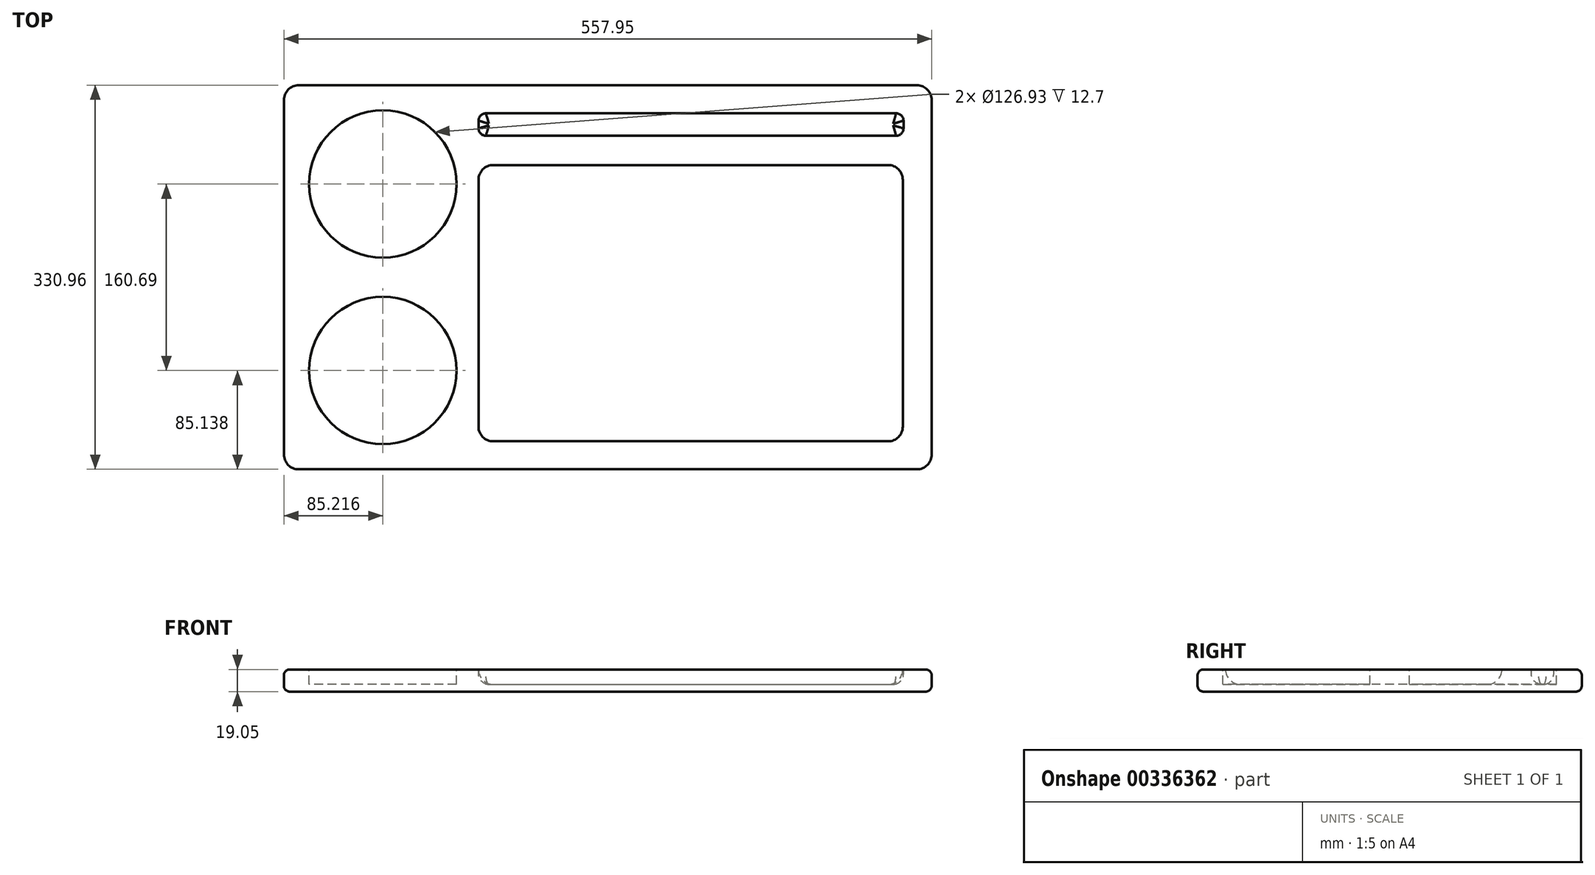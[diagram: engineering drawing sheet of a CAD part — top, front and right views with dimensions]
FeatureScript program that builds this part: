
annotation { "Feature Type Name" : "Feature", "Feature Type Description" : "" }
export const myFeature = defineFeature(function(context is Context, id is Id, definition is map)
    precondition{}
    {
        {
            var Q0;
            Q0=qCreatedBy(makeId("Top.planeOp"),FACE);
            var sketch = newSketch(context, id + "F0", { "sketchPlane" : qUnion([Q0])});
            skLineSegment(sketch, "E0.bottom", {"start": v(-154.97, 103.5) * mm, "end": v(402.98, 103.5) * mm});
            skLineSegment(sketch, "E0.top", {"start": v(-154.97, -227.46) * mm, "end": v(402.98, -227.46) * mm});
            skLineSegment(sketch, "E0.left", {"start": v(-154.97, 103.5) * mm, "end": v(-154.97, -227.46) * mm});
            skLineSegment(sketch, "E0.right", {"start": v(402.98, 103.5) * mm, "end": v(402.98, -227.46) * mm});
            skSolve(sketch);
        }
        {
            var Q0;
            Q0=makeQuery(id+"F0.imprint","IMPRINT",FACE,{"disambiguationData":[TD([[makeQuery(id+"F0.imprint","IMPRINT",EDGE,{"derivedFrom":sQuery(id+"F0.wireOp",EDGE,"E0.top")}),1.0]])]});
            extrude(context, id + "F1", {"entities" : qUnion([Q0]), "depth" : 19.05 * mm});
        }
        {
            var Q0;
            Q0=makeQuery(id+"F1.opExtrude","SWEPT_EDGE",EDGE,{"disambiguationData":[OSD([sQuery(id+"F0.wireOp",EDGE,"E0.top"),sQuery(id+"F0.wireOp",EDGE,"E0.left")])]});
            var Q1;
            Q1=makeQuery(id+"F1.opExtrude","SWEPT_EDGE",EDGE,{"disambiguationData":[OSD([sQuery(id+"F0.wireOp",EDGE,"E0.top"),sQuery(id+"F0.wireOp",EDGE,"E0.right")])]});
            var Q2;
            Q2=makeQuery(id+"F1.opExtrude","SWEPT_EDGE",EDGE,{"disambiguationData":[OSD([sQuery(id+"F0.wireOp",EDGE,"E0.bottom"),sQuery(id+"F0.wireOp",EDGE,"E0.right")])]});
            var Q3;
            Q3=makeQuery(id+"F1.opExtrude","SWEPT_EDGE",EDGE,{"disambiguationData":[OSD([sQuery(id+"F0.wireOp",EDGE,"E0.left"),sQuery(id+"F0.wireOp",EDGE,"E0.bottom")])]});
            fillet(context, id + "F2", {"entities" : qUnion([Q0, Q1, Q2, Q3]), "radius" : 12.7 * mm, "tangentPropagation" : true, "allowEdgeOverflow" : false});
        }
        {
            var Q0;
            Q0=makeQuery(id+"F1.opExtrude","CAP_EDGE",EDGE,{"disambiguationData":[OSD([sQuery(id+"F0.wireOp",EDGE,"E0.right")])],"isStart":false});
            var Q1;
            {var subQ0=sQuery(id+"F0.wireOp",EDGE,"E0.right");var subQ1=sQuery(id+"F0.wireOp",EDGE,"E0.top");Q1=makeQuery(id+"F2.opFillet","BLEND_EDGE",EDGE,{"blendedFrom":[makeQuery(id+"F1.opExtrude","SWEPT_EDGE",EDGE,{"disambiguationData":[OSD([subQ1,subQ0])]}),makeQuery(id+"F1.opExtrude","CAP_FACE",FACE,{"disambiguationData":[OSD([subQ1,sQuery(id+"F0.wireOp",EDGE,"E0.left"),sQuery(id+"F0.wireOp",EDGE,"E0.bottom"),subQ0])],"isStart":false})],"blendedInto":[makeQuery(id+"F1.opExtrude","CAP_FACE",FACE,{"disambiguationData":[OSD([subQ1,sQuery(id+"F0.wireOp",EDGE,"E0.left"),sQuery(id+"F0.wireOp",EDGE,"E0.bottom"),subQ0])],"isStart":false})]});}
            var Q2;
            Q2=makeQuery(id+"F1.opExtrude","CAP_EDGE",EDGE,{"disambiguationData":[OSD([sQuery(id+"F0.wireOp",EDGE,"E0.top")])],"isStart":false});
            var Q3;
            {var subQ0=sQuery(id+"F0.wireOp",EDGE,"E0.left");var subQ1=sQuery(id+"F0.wireOp",EDGE,"E0.top");Q3=makeQuery(id+"F2.opFillet","BLEND_EDGE",EDGE,{"blendedFrom":[makeQuery(id+"F1.opExtrude","SWEPT_EDGE",EDGE,{"disambiguationData":[OSD([subQ1,subQ0])]}),makeQuery(id+"F1.opExtrude","CAP_FACE",FACE,{"disambiguationData":[OSD([subQ1,subQ0,sQuery(id+"F0.wireOp",EDGE,"E0.bottom"),sQuery(id+"F0.wireOp",EDGE,"E0.right")])],"isStart":false})],"blendedInto":[makeQuery(id+"F1.opExtrude","CAP_FACE",FACE,{"disambiguationData":[OSD([subQ1,subQ0,sQuery(id+"F0.wireOp",EDGE,"E0.bottom"),sQuery(id+"F0.wireOp",EDGE,"E0.right")])],"isStart":false})]});}
            var Q4;
            Q4=makeQuery(id+"F1.opExtrude","CAP_EDGE",EDGE,{"disambiguationData":[OSD([sQuery(id+"F0.wireOp",EDGE,"E0.left")])],"isStart":false});
            var Q5;
            {var subQ0=sQuery(id+"F0.wireOp",EDGE,"E0.bottom");var subQ1=sQuery(id+"F0.wireOp",EDGE,"E0.left");Q5=makeQuery(id+"F2.opFillet","BLEND_EDGE",EDGE,{"blendedFrom":[makeQuery(id+"F1.opExtrude","SWEPT_EDGE",EDGE,{"disambiguationData":[OSD([subQ1,subQ0])]}),makeQuery(id+"F1.opExtrude","CAP_FACE",FACE,{"disambiguationData":[OSD([sQuery(id+"F0.wireOp",EDGE,"E0.top"),subQ1,subQ0,sQuery(id+"F0.wireOp",EDGE,"E0.right")])],"isStart":false})],"blendedInto":[makeQuery(id+"F1.opExtrude","CAP_FACE",FACE,{"disambiguationData":[OSD([sQuery(id+"F0.wireOp",EDGE,"E0.top"),subQ1,subQ0,sQuery(id+"F0.wireOp",EDGE,"E0.right")])],"isStart":false})]});}
            var Q6;
            Q6=makeQuery(id+"F1.opExtrude","CAP_EDGE",EDGE,{"disambiguationData":[OSD([sQuery(id+"F0.wireOp",EDGE,"E0.bottom")])],"isStart":false});
            var Q7;
            {var subQ0=sQuery(id+"F0.wireOp",EDGE,"E0.right");var subQ1=sQuery(id+"F0.wireOp",EDGE,"E0.bottom");Q7=makeQuery(id+"F2.opFillet","BLEND_EDGE",EDGE,{"blendedFrom":[makeQuery(id+"F1.opExtrude","SWEPT_EDGE",EDGE,{"disambiguationData":[OSD([subQ1,subQ0])]}),makeQuery(id+"F1.opExtrude","CAP_FACE",FACE,{"disambiguationData":[OSD([sQuery(id+"F0.wireOp",EDGE,"E0.top"),sQuery(id+"F0.wireOp",EDGE,"E0.left"),subQ1,subQ0])],"isStart":false})],"blendedInto":[makeQuery(id+"F1.opExtrude","CAP_FACE",FACE,{"disambiguationData":[OSD([sQuery(id+"F0.wireOp",EDGE,"E0.top"),sQuery(id+"F0.wireOp",EDGE,"E0.left"),subQ1,subQ0])],"isStart":false})]});}
            var Q8;
            Q8=makeQuery(id+"F1.opExtrude","CAP_EDGE",EDGE,{"disambiguationData":[OSD([sQuery(id+"F0.wireOp",EDGE,"E0.bottom")])],"isStart":true});
            var Q9;
            {var subQ0=sQuery(id+"F0.wireOp",EDGE,"E0.right");var subQ1=sQuery(id+"F0.wireOp",EDGE,"E0.bottom");Q9=makeQuery(id+"F2.opFillet","BLEND_EDGE",EDGE,{"blendedFrom":[makeQuery(id+"F1.opExtrude","SWEPT_EDGE",EDGE,{"disambiguationData":[OSD([subQ1,subQ0])]}),makeQuery(id+"F1.opExtrude","CAP_FACE",FACE,{"disambiguationData":[OSD([sQuery(id+"F0.wireOp",EDGE,"E0.top"),sQuery(id+"F0.wireOp",EDGE,"E0.left"),subQ1,subQ0])],"isStart":true})],"blendedInto":[makeQuery(id+"F1.opExtrude","CAP_FACE",FACE,{"disambiguationData":[OSD([sQuery(id+"F0.wireOp",EDGE,"E0.top"),sQuery(id+"F0.wireOp",EDGE,"E0.left"),subQ1,subQ0])],"isStart":true})]});}
            var Q10;
            Q10=makeQuery(id+"F1.opExtrude","CAP_EDGE",EDGE,{"disambiguationData":[OSD([sQuery(id+"F0.wireOp",EDGE,"E0.right")])],"isStart":true});
            var Q11;
            {var subQ0=sQuery(id+"F0.wireOp",EDGE,"E0.right");var subQ1=sQuery(id+"F0.wireOp",EDGE,"E0.top");Q11=makeQuery(id+"F2.opFillet","BLEND_EDGE",EDGE,{"blendedFrom":[makeQuery(id+"F1.opExtrude","SWEPT_EDGE",EDGE,{"disambiguationData":[OSD([subQ1,subQ0])]}),makeQuery(id+"F1.opExtrude","CAP_FACE",FACE,{"disambiguationData":[OSD([subQ1,sQuery(id+"F0.wireOp",EDGE,"E0.left"),sQuery(id+"F0.wireOp",EDGE,"E0.bottom"),subQ0])],"isStart":true})],"blendedInto":[makeQuery(id+"F1.opExtrude","CAP_FACE",FACE,{"disambiguationData":[OSD([subQ1,sQuery(id+"F0.wireOp",EDGE,"E0.left"),sQuery(id+"F0.wireOp",EDGE,"E0.bottom"),subQ0])],"isStart":true})]});}
            var Q12;
            Q12=makeQuery(id+"F1.opExtrude","CAP_EDGE",EDGE,{"disambiguationData":[OSD([sQuery(id+"F0.wireOp",EDGE,"E0.top")])],"isStart":true});
            var Q13;
            Q13=makeQuery(id+"F1.opExtrude","CAP_EDGE",EDGE,{"disambiguationData":[OSD([sQuery(id+"F0.wireOp",EDGE,"E0.left")])],"isStart":true});
            var Q14;
            {var subQ0=sQuery(id+"F0.wireOp",EDGE,"E0.left");var subQ1=sQuery(id+"F0.wireOp",EDGE,"E0.top");Q14=makeQuery(id+"F2.opFillet","BLEND_EDGE",EDGE,{"blendedFrom":[makeQuery(id+"F1.opExtrude","SWEPT_EDGE",EDGE,{"disambiguationData":[OSD([subQ1,subQ0])]}),makeQuery(id+"F1.opExtrude","CAP_FACE",FACE,{"disambiguationData":[OSD([subQ1,subQ0,sQuery(id+"F0.wireOp",EDGE,"E0.bottom"),sQuery(id+"F0.wireOp",EDGE,"E0.right")])],"isStart":true})],"blendedInto":[makeQuery(id+"F1.opExtrude","CAP_FACE",FACE,{"disambiguationData":[OSD([subQ1,subQ0,sQuery(id+"F0.wireOp",EDGE,"E0.bottom"),sQuery(id+"F0.wireOp",EDGE,"E0.right")])],"isStart":true})]});}
            var Q15;
            {var subQ0=sQuery(id+"F0.wireOp",EDGE,"E0.bottom");var subQ1=sQuery(id+"F0.wireOp",EDGE,"E0.left");Q15=makeQuery(id+"F2.opFillet","BLEND_EDGE",EDGE,{"blendedFrom":[makeQuery(id+"F1.opExtrude","SWEPT_EDGE",EDGE,{"disambiguationData":[OSD([subQ1,subQ0])]}),makeQuery(id+"F1.opExtrude","CAP_FACE",FACE,{"disambiguationData":[OSD([sQuery(id+"F0.wireOp",EDGE,"E0.top"),subQ1,subQ0,sQuery(id+"F0.wireOp",EDGE,"E0.right")])],"isStart":true})],"blendedInto":[makeQuery(id+"F1.opExtrude","CAP_FACE",FACE,{"disambiguationData":[OSD([sQuery(id+"F0.wireOp",EDGE,"E0.top"),subQ1,subQ0,sQuery(id+"F0.wireOp",EDGE,"E0.right")])],"isStart":true})]});}
            fillet(context, id + "F3", {"entities" : qUnion([Q0, Q1, Q2, Q3, Q4, Q5, Q6, Q7, Q8, Q9, Q10, Q11, Q12, Q13, Q14, Q15]), "radius" : 5.08 * mm, "tangentPropagation" : true, "allowEdgeOverflow" : false});
        }
        {
            var Q0;
            Q0=makeQuery(id+"F1.opExtrude","CAP_FACE",FACE,{"disambiguationData":[OSD([sQuery(id+"F0.wireOp",EDGE,"E0.top"),sQuery(id+"F0.wireOp",EDGE,"E0.left"),sQuery(id+"F0.wireOp",EDGE,"E0.bottom"),sQuery(id+"F0.wireOp",EDGE,"E0.right")])],"isStart":false});
            var sketch = newSketch(context, id + "F4", { "sketchPlane" : qUnion([Q0])});
            skLineSegment(sketch, "E1", {"start": v(-149.9, -61.98) * mm, "end": v(-124.2, -61.98) * mm});
            skPoint(sketch, "E1.endSnap0", {"position": v(-149.9, -61.98) * mm});
            skLineSegment(sketch, "E2", {"start": v(-124.2, -61.98) * mm, "end": v(-15.31, -61.98) * mm});
            skLineSegment(sketch, "E3", {"start": v(-69.75, -61.98) * mm, "end": v(-69.75, -45.1) * mm});
            skLineSegment(sketch, "E4", {"start": v(-69.75, -45.1) * mm, "end": v(-69.75, 18.37) * mm});
            skLineSegment(sketch, "E5.MirrorCS", {"start": v(-69.75, -78.86) * mm, "end": v(-69.75, -142.32) * mm});
            skLineSegment(sketch, "E6.MirrorCS", {"start": v(-69.75, -61.98) * mm, "end": v(-69.75, -78.86) * mm});
            skCircle(sketch, "E7", {"center": v(-69.75, 18.37) * mm, "radius": 63.46 * mm});
            skCircle(sketch, "E8", {"center": v(-69.75, -142.32) * mm, "radius": 63.46 * mm});
            skSolve(sketch);
        }
        {
            var Q0;
            Q0=makeQuery(id+"F4.imprint","IMPRINT",FACE,{"disambiguationData":[TD([[makeQuery(id+"F4.imprint","IMPRINT",EDGE,{"derivedFrom":sQuery(id+"F4.wireOp",EDGE,"E8")}),1.0]])]});
            var Q1;
            Q1=makeQuery(id+"F4.imprint","IMPRINT",FACE,{"disambiguationData":[TD([[makeQuery(id+"F4.imprint","IMPRINT",EDGE,{"derivedFrom":sQuery(id+"F4.wireOp",EDGE,"E7")}),1.0]])]});
            extrude(context, id + "F5", {"entities" : qUnion([Q0, Q1]), "operationType" : NewBodyOperationType.REMOVE, "oppositeDirection" : true, "depth" : 12.7 * mm});
        }
        {
            var Q0;
            Q0=makeQuery(id+"F1.opExtrude","CAP_FACE",FACE,{"disambiguationData":[OSD([sQuery(id+"F0.wireOp",EDGE,"E0.top"),sQuery(id+"F0.wireOp",EDGE,"E0.left"),sQuery(id+"F0.wireOp",EDGE,"E0.bottom"),sQuery(id+"F0.wireOp",EDGE,"E0.right")])],"isStart":false});
            var sketch = newSketch(context, id + "F6", { "sketchPlane" : qUnion([Q0])});
            skLineSegment(sketch, "E9", {"start": v(397.9, -214.76) * mm, "end": v(378.08, -214.76) * mm});
            skLineSegment(sketch, "E10", {"start": v(378.08, -214.76) * mm, "end": v(378.08, -222.38) * mm});
            skLineSegment(sketch, "E11", {"start": v(378.08, -222.38) * mm, "end": v(378.08, -203.34) * mm});
            skLineSegment(sketch, "E12", {"start": v(397.9, 90.8) * mm, "end": v(378.7, 90.8) * mm});
            skLineSegment(sketch, "E13", {"start": v(378.7, 90.8) * mm, "end": v(378.7, 98.42) * mm});
            skLineSegment(sketch, "E14", {"start": v(378.7, 98.42) * mm, "end": v(378.7, 79.3) * mm});
            skLineSegment(sketch, "E15", {"start": v(378.7, 79.3) * mm, "end": v(-10.3, 79.3) * mm});
            skLineSegment(sketch, "E16", {"start": v(12.66, 79.3) * mm, "end": v(12.66, 60.01) * mm});
            skLineSegment(sketch, "E17.bottom", {"start": v(19, 60.01) * mm, "end": v(372.35, 60.01) * mm});
            skLineSegment(sketch, "E17.top", {"start": v(19, 79.3) * mm, "end": v(372.35, 79.3) * mm});
            skLineSegment(sketch, "E17.left", {"start": v(12.66, 66.36) * mm, "end": v(12.66, 72.96) * mm});
            skLineSegment(sketch, "E17.right", {"start": v(378.7, 66.36) * mm, "end": v(378.7, 72.96) * mm});
            skLineSegment(sketch, "E18.bottom", {"start": v(25.36, 34.72) * mm, "end": v(365.38, 34.72) * mm});
            skLineSegment(sketch, "E18.top", {"start": v(25.36, -203.34) * mm, "end": v(365.38, -203.34) * mm});
            skLineSegment(sketch, "E18.left", {"start": v(12.66, 22.02) * mm, "end": v(12.66, -190.64) * mm});
            skLineSegment(sketch, "E18.right", {"start": v(378.08, 22.02) * mm, "end": v(378.08, -190.64) * mm});
            skPoint(sketch, "E19.visualSharp", {"position": v(12.66, 79.3) * mm});
            skArc(sketch, "E19.filletArc", {"start": v(19, 79.3) * mm, "mid": v(14.52, 77.45) * mm, "end": v(12.66, 72.96) * mm});
            skPoint(sketch, "E20.visualSharp", {"position": v(12.66, 60.01) * mm});
            skArc(sketch, "E20.filletArc", {"start": v(12.66, 66.36) * mm, "mid": v(14.52, 61.87) * mm, "end": v(19, 60.01) * mm});
            skPoint(sketch, "E21.visualSharp", {"position": v(378.7, 79.3) * mm});
            skArc(sketch, "E21.filletArc", {"start": v(378.7, 72.96) * mm, "mid": v(376.84, 77.45) * mm, "end": v(372.35, 79.3) * mm});
            skPoint(sketch, "E22.visualSharp", {"position": v(378.7, 60.01) * mm});
            skArc(sketch, "E22.filletArc", {"start": v(372.35, 60.01) * mm, "mid": v(376.84, 61.87) * mm, "end": v(378.7, 66.36) * mm});
            skPoint(sketch, "E23.visualSharp", {"position": v(12.66, 34.72) * mm});
            skArc(sketch, "E23.filletArc", {"start": v(25.36, 34.72) * mm, "mid": v(16.38, 31) * mm, "end": v(12.66, 22.02) * mm});
            skPoint(sketch, "E24.visualSharp", {"position": v(378.08, 34.72) * mm});
            skArc(sketch, "E24.filletArc", {"start": v(378.08, 22.02) * mm, "mid": v(374.36, 31) * mm, "end": v(365.38, 34.72) * mm});
            skPoint(sketch, "E25.visualSharp", {"position": v(378.08, -203.34) * mm});
            skArc(sketch, "E25.filletArc", {"start": v(365.38, -203.34) * mm, "mid": v(374.36, -199.62) * mm, "end": v(378.08, -190.64) * mm});
            skPoint(sketch, "E26.visualSharp", {"position": v(12.66, -203.34) * mm});
            skArc(sketch, "E26.filletArc", {"start": v(12.66, -190.64) * mm, "mid": v(16.38, -199.62) * mm, "end": v(25.36, -203.34) * mm});
            skSolve(sketch);
        }
        {
            var Q0;
            Q0=makeQuery(id+"F6.imprint","IMPRINT",FACE,{"disambiguationData":[TD([[makeQuery(id+"F6.imprint","IMPRINT",EDGE,{"derivedFrom":sQuery(id+"F6.wireOp",EDGE,"E17.bottom")}),1.0]])]});
            var Q1;
            Q1=makeQuery(id+"F6.imprint","IMPRINT",FACE,{"disambiguationData":[TD([[makeQuery(id+"F6.imprint","IMPRINT",EDGE,{"derivedFrom":sQuery(id+"F6.wireOp",EDGE,"E18.bottom")}),-1.0]])]});
            extrude(context, id + "F7", {"entities" : qUnion([Q0, Q1]), "operationType" : NewBodyOperationType.REMOVE, "oppositeDirection" : true, "depth" : 12.7 * mm});
        }
        {
            var Q0;
            Q0=makeQuery(id+"F7.boolean.opBoolean","COPY",FACE,{"derivedFrom":makeQuery(id+"F7.opExtrude","CAP_FACE",FACE,{"disambiguationData":[OSD([sQuery(id+"F6.wireOp",EDGE,"E17.bottom"),sQuery(id+"F6.wireOp",EDGE,"E17.top"),sQuery(id+"F6.wireOp",EDGE,"E17.left"),sQuery(id+"F6.wireOp",EDGE,"E17.right"),sQuery(id+"F6.wireOp",EDGE,"E19.filletArc"),sQuery(id+"F6.wireOp",EDGE,"E20.filletArc"),sQuery(id+"F6.wireOp",EDGE,"E21.filletArc"),sQuery(id+"F6.wireOp",EDGE,"E22.filletArc")])],"isStart":false})});
            fillet(context, id + "F8", {"entities" : qUnion([Q0]), "radius" : 8.9 * mm, "tangentPropagation" : true, "allowEdgeOverflow" : false});
        }
        {
            var Q0;
            Q0=makeQuery(id+"F7.boolean.opBoolean","COPY",FACE,{"derivedFrom":makeQuery(id+"F7.opExtrude","CAP_FACE",FACE,{"disambiguationData":[OSD([sQuery(id+"F6.wireOp",EDGE,"E18.bottom"),sQuery(id+"F6.wireOp",EDGE,"E18.top"),sQuery(id+"F6.wireOp",EDGE,"E18.left"),sQuery(id+"F6.wireOp",EDGE,"E18.right"),sQuery(id+"F6.wireOp",EDGE,"E23.filletArc"),sQuery(id+"F6.wireOp",EDGE,"E24.filletArc"),sQuery(id+"F6.wireOp",EDGE,"E25.filletArc"),sQuery(id+"F6.wireOp",EDGE,"E26.filletArc")])],"isStart":false})});
            fillet(context, id + "F9", {"entities" : qUnion([Q0]), "radius" : 12.7 * mm, "tangentPropagation" : true, "allowEdgeOverflow" : false});
        }
    });
